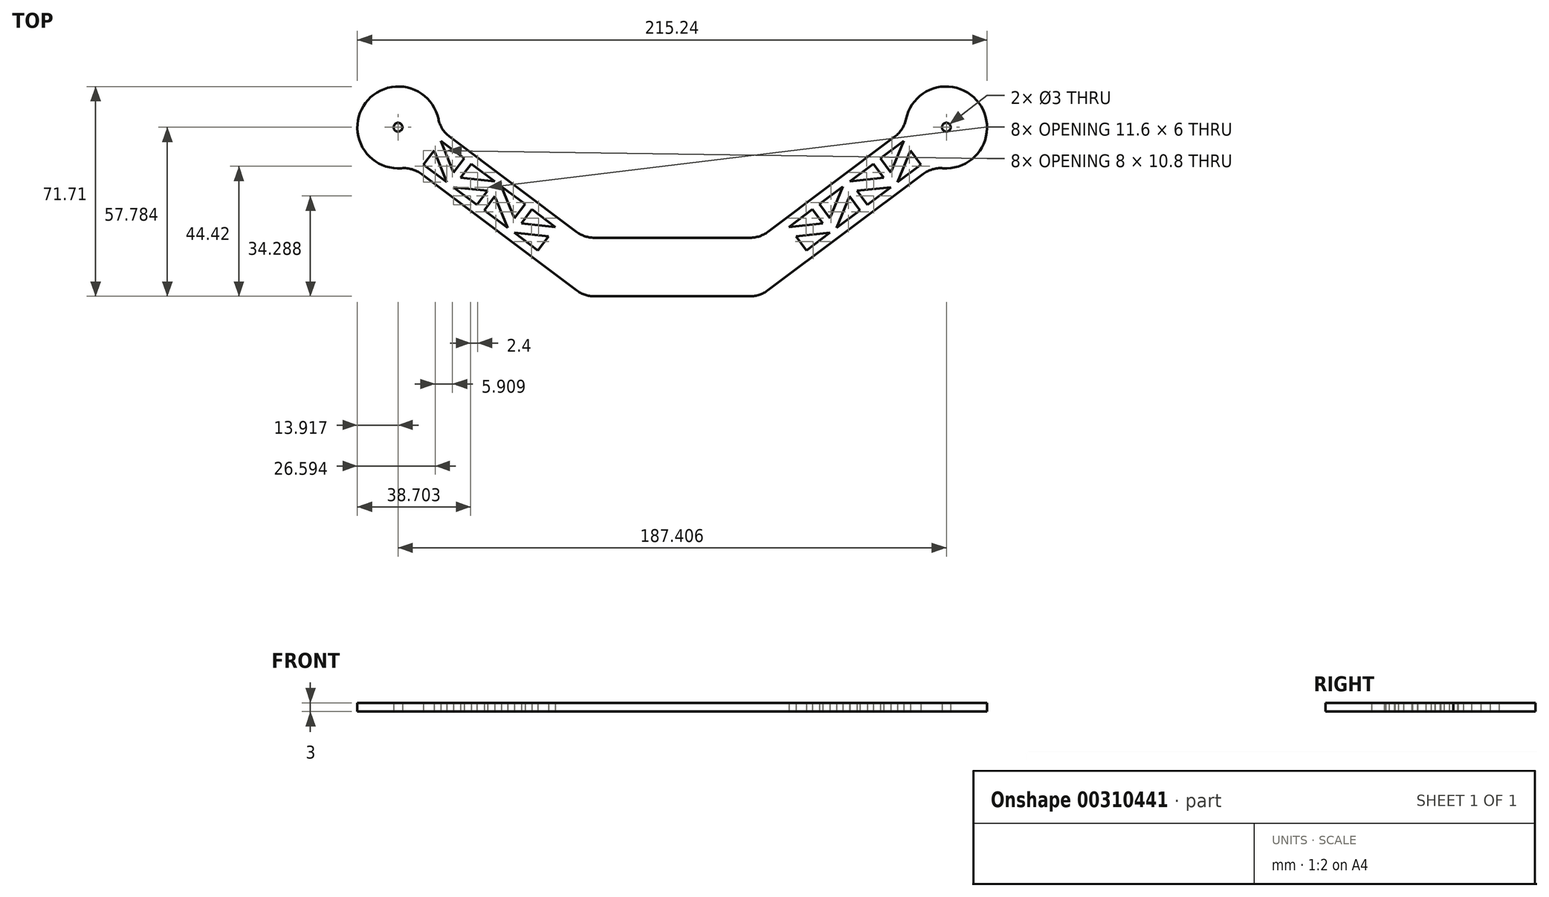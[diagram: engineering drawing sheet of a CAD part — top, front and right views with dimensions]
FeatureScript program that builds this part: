
annotation { "Feature Type Name" : "Feature", "Feature Type Description" : "" }
export const myFeature = defineFeature(function(context is Context, id is Id, definition is map)
    precondition{}
    {
        {
            var Q0;
            Q0=qCreatedBy(makeId("Top.planeOp"),FACE);
            var sketch = newSketch(context, id + "F0", { "sketchPlane" : qUnion([Q0])});
            skLineSegment(sketch, "E0.MirrorCS", {"start": v(-26.67, 20) * mm, "end": v(0, 20) * mm});
            skLineSegment(sketch, "E1.MirrorCS", {"start": v(0, 0) * mm, "end": v(-26.67, 0) * mm});
            skLineSegment(sketch, "E2.MirrorCS", {"start": v(-32.67, 2) * mm, "end": v(-89.23, 44.42) * mm});
            skLineSegment(sketch, "E3.MirrorCS", {"start": v(-79.63, 57.22) * mm, "end": v(-30, 20) * mm});
            skArc(sketch, "E4.MirrorCS", {"start": v(-92.5, 43.76) * mm, "mid": v(-104.82, 66.11) * mm, "end": v(-79.9, 60.56) * mm});
            skCircle(sketch, "E5.MirrorC", {"center": v(-93.7, 57.78) * mm, "radius": 1.5 * mm});
            skLineSegment(sketch, "E6.MirrorCS", {"start": v(-89.23, 44.42) * mm, "end": v(-39.6, 7.2) * mm});
            skLineSegment(sketch, "E7.MirrorCS", {"start": v(-32.67, 22) * mm, "end": v(-76.12, 54.59) * mm});
            skLineSegment(sketch, "E8", {"start": v(-93.7, 57.78) * mm, "end": v(-87.3, 52.98) * mm});
            skLineSegment(sketch, "E9", {"start": v(-93.7, 57.78) * mm, "end": v(-88.9, 64.18) * mm});
            skLineSegment(sketch, "E10", {"start": v(-93.7, 57.78) * mm, "end": v(-100.1, 62.58) * mm});
            skLineSegment(sketch, "E11", {"start": v(-93.7, 57.78) * mm, "end": v(-98.5, 51.38) * mm});
            skPoint(sketch, "E12.orphan", {"position": v(-92.1, 46.58) * mm});
            skPoint(sketch, "E13.orphan", {"position": v(-82.5, 59.38) * mm});
            skLineSegment(sketch, "E14", {"start": v(0, 0) * mm, "end": v(0, 75.2) * mm});
            skLineSegment(sketch, "E15", {"start": v(0, 20) * mm, "end": v(0, 0) * mm});
            skLineSegment(sketch, "E16", {"start": v(0, 10) * mm, "end": v(-5, 10) * mm});
            skLineSegment(sketch, "E17", {"start": v(-5, 10) * mm, "end": v(-5, 15) * mm});
            skLineSegment(sketch, "E18", {"start": v(-5, 10) * mm, "end": v(-5, 5) * mm});
            skLineSegment(sketch, "E19", {"start": v(-86.83, 42.62) * mm, "end": v(-85.72, 41.79) * mm});
            skLineSegment(sketch, "E20", {"start": v(-71.72, 51.29) * mm, "end": v(-70.12, 50.09) * mm});
            skLineSegment(sketch, "E21", {"start": v(-79.63, 57.22) * mm, "end": v(-77.23, 55.42) * mm});
            skLineSegment(sketch, "E22", {"start": v(-85.03, 45.02) * mm, "end": v(-77.03, 39.02) * mm});
            skLineSegment(sketch, "E23", {"start": v(-85.03, 45.02) * mm, "end": v(-81.43, 49.82) * mm});
            skLineSegment(sketch, "E24", {"start": v(-81.43, 49.82) * mm, "end": v(-77.03, 39.02) * mm});
            skLineSegment(sketch, "E25", {"start": v(-74.72, 42.29) * mm, "end": v(-79.12, 53.09) * mm});
            skLineSegment(sketch, "E26", {"start": v(-74.72, 42.29) * mm, "end": v(-71.12, 47.09) * mm});
            skLineSegment(sketch, "E27", {"start": v(-79.12, 53.09) * mm, "end": v(-71.12, 47.09) * mm});
            skLineSegment(sketch, "E28", {"start": v(-77.03, 39.02) * mm, "end": v(-75.83, 38.12) * mm});
            skLineSegment(sketch, "E29.MirrorCS", {"start": v(-72.32, 40.49) * mm, "end": v(-68.72, 45.29) * mm});
            skLineSegment(sketch, "E30.MirrorCS", {"start": v(-60.72, 39.29) * mm, "end": v(-68.72, 45.29) * mm});
            skLineSegment(sketch, "E31.MirrorCS", {"start": v(-72.32, 40.49) * mm, "end": v(-60.72, 39.29) * mm});
            skLineSegment(sketch, "E32.MirrorCS", {"start": v(-63.12, 36.09) * mm, "end": v(-74.72, 37.29) * mm});
            skLineSegment(sketch, "E33.MirrorCS", {"start": v(-66.72, 31.29) * mm, "end": v(-63.12, 36.09) * mm});
            skLineSegment(sketch, "E34", {"start": v(-74.72, 37.29) * mm, "end": v(-66.72, 31.29) * mm});
            skLineSegment(sketch, "E35", {"start": v(-66.72, 31.29) * mm, "end": v(-64.32, 29.49) * mm});
            skLineSegment(sketch, "E36.1.0.0", {"start": v(-51.52, 24.89) * mm, "end": v(-39.92, 23.69) * mm});
            skLineSegment(sketch, "E36.1.0.1", {"start": v(-39.92, 23.69) * mm, "end": v(-47.92, 29.69) * mm});
            skLineSegment(sketch, "E36.1.0.2", {"start": v(-51.52, 24.89) * mm, "end": v(-47.92, 29.69) * mm});
            skLineSegment(sketch, "E36.1.0.3", {"start": v(-42.32, 20.49) * mm, "end": v(-53.92, 21.69) * mm});
            skLineSegment(sketch, "E36.1.0.4", {"start": v(-53.92, 21.69) * mm, "end": v(-45.92, 15.69) * mm});
            skLineSegment(sketch, "E36.1.0.5", {"start": v(-45.92, 15.69) * mm, "end": v(-42.32, 20.49) * mm});
            skLineSegment(sketch, "E36.1.0.6", {"start": v(-53.92, 26.69) * mm, "end": v(-50.32, 31.49) * mm});
            skLineSegment(sketch, "E36.1.0.7", {"start": v(-53.92, 26.69) * mm, "end": v(-58.32, 37.49) * mm});
            skLineSegment(sketch, "E36.1.0.8", {"start": v(-60.63, 34.22) * mm, "end": v(-56.23, 23.42) * mm});
            skLineSegment(sketch, "E36.1.0.9", {"start": v(-64.23, 29.42) * mm, "end": v(-56.23, 23.42) * mm});
            skLineSegment(sketch, "E36.1.0.10", {"start": v(-64.23, 29.42) * mm, "end": v(-60.63, 34.22) * mm});
            skLineSegment(sketch, "E36.1.0.11", {"start": v(-58.32, 37.49) * mm, "end": v(-50.32, 31.49) * mm});
            skLineSegment(sketch, "E36.direction1", {"start": v(-85.03, 45.02) * mm, "end": v(-64.23, 29.42) * mm, "construction": true});
            skLineSegment(sketch, "E37.MirrorCS", {"start": v(77.23, 55.42) * mm, "end": v(76.12, 54.59) * mm});
            skLineSegment(sketch, "E38.MirrorCS", {"start": v(86.83, 42.62) * mm, "end": v(85.72, 41.79) * mm});
            skCircle(sketch, "E39.MirrorC", {"center": v(93.7, 57.78) * mm, "radius": 1.5 * mm});
            skLineSegment(sketch, "E40.MirrorCS", {"start": v(77.03, 39.02) * mm, "end": v(75.83, 38.12) * mm});
            skLineSegment(sketch, "E41.MirrorCS", {"start": v(66.72, 31.29) * mm, "end": v(64.32, 29.49) * mm});
            skLineSegment(sketch, "E42.MirrorCS", {"start": v(85.03, 45.02) * mm, "end": v(81.43, 49.82) * mm});
            skLineSegment(sketch, "E43.MirrorCS", {"start": v(74.72, 42.29) * mm, "end": v(71.12, 47.09) * mm});
            skLineSegment(sketch, "E44.MirrorCS", {"start": v(66.72, 31.29) * mm, "end": v(63.12, 36.09) * mm});
            skLineSegment(sketch, "E45.MirrorCS", {"start": v(53.92, 21.69) * mm, "end": v(45.92, 15.69) * mm});
            skLineSegment(sketch, "E46.MirrorCS", {"start": v(72.32, 40.49) * mm, "end": v(68.72, 45.29) * mm});
            skLineSegment(sketch, "E47.MirrorCS", {"start": v(53.92, 26.69) * mm, "end": v(50.32, 31.49) * mm});
            skLineSegment(sketch, "E48.MirrorCS", {"start": v(64.23, 29.42) * mm, "end": v(60.63, 34.22) * mm});
            skLineSegment(sketch, "E49.MirrorCS", {"start": v(51.52, 24.89) * mm, "end": v(47.92, 29.69) * mm});
            skLineSegment(sketch, "E50.MirrorCS", {"start": v(45.92, 15.69) * mm, "end": v(42.32, 20.49) * mm});
            skLineSegment(sketch, "E51.MirrorCS", {"start": v(79.63, 57.22) * mm, "end": v(32.67, 22) * mm});
            skLineSegment(sketch, "E52.MirrorCS", {"start": v(85.03, 45.02) * mm, "end": v(77.03, 39.02) * mm});
            skLineSegment(sketch, "E53.MirrorCS", {"start": v(93.7, 57.78) * mm, "end": v(88.9, 64.18) * mm});
            skLineSegment(sketch, "E54.MirrorCS", {"start": v(79.12, 53.09) * mm, "end": v(71.12, 47.09) * mm});
            skLineSegment(sketch, "E55.MirrorCS", {"start": v(0, 10) * mm, "end": v(5, 10) * mm});
            skLineSegment(sketch, "E56.MirrorCS", {"start": v(5, 10) * mm, "end": v(5, 15) * mm});
            skLineSegment(sketch, "E57.MirrorCS", {"start": v(93.7, 57.78) * mm, "end": v(100.1, 62.58) * mm});
            skLineSegment(sketch, "E58.MirrorCS", {"start": v(93.7, 57.78) * mm, "end": v(98.5, 51.38) * mm});
            skLineSegment(sketch, "E59.MirrorCS", {"start": v(74.72, 37.29) * mm, "end": v(66.72, 31.29) * mm});
            skLineSegment(sketch, "E60.MirrorCS", {"start": v(93.7, 57.78) * mm, "end": v(87.3, 52.98) * mm});
            skLineSegment(sketch, "E61.MirrorCS", {"start": v(5, 10) * mm, "end": v(5, 5) * mm});
            skLineSegment(sketch, "E62.MirrorCS", {"start": v(71.72, 51.29) * mm, "end": v(70.12, 50.09) * mm});
            skLineSegment(sketch, "E63.MirrorCS", {"start": v(30, 20) * mm, "end": v(79.63, 57.22) * mm});
            skLineSegment(sketch, "E64.MirrorCS", {"start": v(53.92, 26.69) * mm, "end": v(58.32, 37.49) * mm});
            skLineSegment(sketch, "E65.MirrorCS", {"start": v(89.23, 44.42) * mm, "end": v(39.6, 7.2) * mm});
            skLineSegment(sketch, "E66.MirrorCS", {"start": v(32.67, 2) * mm, "end": v(89.23, 44.42) * mm});
            skLineSegment(sketch, "E67.MirrorCS", {"start": v(51.52, 24.89) * mm, "end": v(39.92, 23.69) * mm});
            skLineSegment(sketch, "E68.MirrorCS", {"start": v(63.12, 36.09) * mm, "end": v(74.72, 37.29) * mm});
            skPoint(sketch, "E69.MirrorP", {"position": v(82.5, 59.38) * mm});
            skPoint(sketch, "E70.MirrorP", {"position": v(92.1, 46.58) * mm});
            skLineSegment(sketch, "E71.MirrorCS", {"start": v(72.32, 40.49) * mm, "end": v(60.72, 39.29) * mm});
            skLineSegment(sketch, "E72.MirrorCS", {"start": v(0, 0) * mm, "end": v(26.67, 0) * mm});
            skLineSegment(sketch, "E73.MirrorCS", {"start": v(39.92, 23.69) * mm, "end": v(47.92, 29.69) * mm});
            skLineSegment(sketch, "E74.MirrorCS", {"start": v(81.43, 49.82) * mm, "end": v(77.03, 39.02) * mm});
            skLineSegment(sketch, "E75.MirrorCS", {"start": v(60.72, 39.29) * mm, "end": v(68.72, 45.29) * mm});
            skArc(sketch, "E76.MirrorCS", {"start": v(92.5, 43.76) * mm, "mid": v(104.82, 66.11) * mm, "end": v(79.9, 60.56) * mm});
            skLineSegment(sketch, "E77.MirrorCS", {"start": v(26.67, 20) * mm, "end": v(0, 20) * mm});
            skLineSegment(sketch, "E78.MirrorCS", {"start": v(58.32, 37.49) * mm, "end": v(50.32, 31.49) * mm});
            skLineSegment(sketch, "E79.MirrorCS", {"start": v(74.72, 42.29) * mm, "end": v(79.12, 53.09) * mm});
            skLineSegment(sketch, "E80.MirrorCS", {"start": v(85.03, 45.02) * mm, "end": v(64.23, 29.42) * mm, "construction": true});
            skLineSegment(sketch, "E81.MirrorCS", {"start": v(60.63, 34.22) * mm, "end": v(56.23, 23.42) * mm});
            skLineSegment(sketch, "E82.MirrorCS", {"start": v(42.32, 20.49) * mm, "end": v(53.92, 21.69) * mm});
            skLineSegment(sketch, "E83.MirrorCS", {"start": v(64.23, 29.42) * mm, "end": v(56.23, 23.42) * mm});
            skLineSegment(sketch, "E84", {"start": v(-30, 20) * mm, "end": v(-30, 0) * mm});
            skLineSegment(sketch, "E85", {"start": v(30, 20) * mm, "end": v(30, 0) * mm});
            skPoint(sketch, "E86.visualSharp", {"position": v(-30, 20) * mm});
            skArc(sketch, "E86.filletArc", {"start": v(-32.67, 22) * mm, "mid": v(-29.83, 20.51) * mm, "end": v(-26.67, 20) * mm});
            skPoint(sketch, "E87.visualSharp", {"position": v(-30, 0) * mm});
            skArc(sketch, "E87.filletArc", {"start": v(-32.67, 2) * mm, "mid": v(-29.83, 0.51) * mm, "end": v(-26.67, 0) * mm});
            skPoint(sketch, "E88.visualSharp", {"position": v(-89.23, 44.42) * mm});
            skArc(sketch, "E88.filletArc", {"start": v(-85.72, 41.79) * mm, "mid": v(-88.93, 43.4) * mm, "end": v(-92.5, 43.76) * mm});
            skPoint(sketch, "E89.visualSharp", {"position": v(-79.63, 57.22) * mm});
            skArc(sketch, "E89.filletArc", {"start": v(-79.9, 60.56) * mm, "mid": v(-78.56, 57.23) * mm, "end": v(-76.12, 54.59) * mm});
            skPoint(sketch, "E90.visualSharp", {"position": v(30, 20) * mm});
            skArc(sketch, "E90.filletArc", {"start": v(26.67, 20) * mm, "mid": v(29.83, 20.51) * mm, "end": v(32.67, 22) * mm});
            skPoint(sketch, "E91.visualSharp", {"position": v(30, 0) * mm});
            skArc(sketch, "E91.filletArc", {"start": v(26.67, 0) * mm, "mid": v(29.83, 0.51) * mm, "end": v(32.67, 2) * mm});
            skPoint(sketch, "E92.visualSharp", {"position": v(79.63, 57.22) * mm});
            skArc(sketch, "E92.filletArc", {"start": v(76.12, 54.59) * mm, "mid": v(78.56, 57.23) * mm, "end": v(79.9, 60.56) * mm});
            skPoint(sketch, "E93.visualSharp", {"position": v(89.23, 44.42) * mm});
            skArc(sketch, "E93.filletArc", {"start": v(92.5, 43.76) * mm, "mid": v(88.93, 43.4) * mm, "end": v(85.72, 41.79) * mm});
            skSolve(sketch);
        }
        {
            var Q0;
            Q0 = qSketchRegion(id + "F0", true);
            var Q1;
            Q1=makeQuery(id+"F0.imprint","IMPRINT",FACE,{"disambiguationData":[TD([[makeQuery(id+"F0.imprint","IMPRINT",EDGE,{"derivedFrom":sQuery(id+"F0.wireOp",EDGE,"E0.MirrorCS")}),-1.0]])]});
            extrude(context, id + "F1", {"entities" : qUnion([Q0, Q1]), "depth" : 3 * mm});
        }
    });
